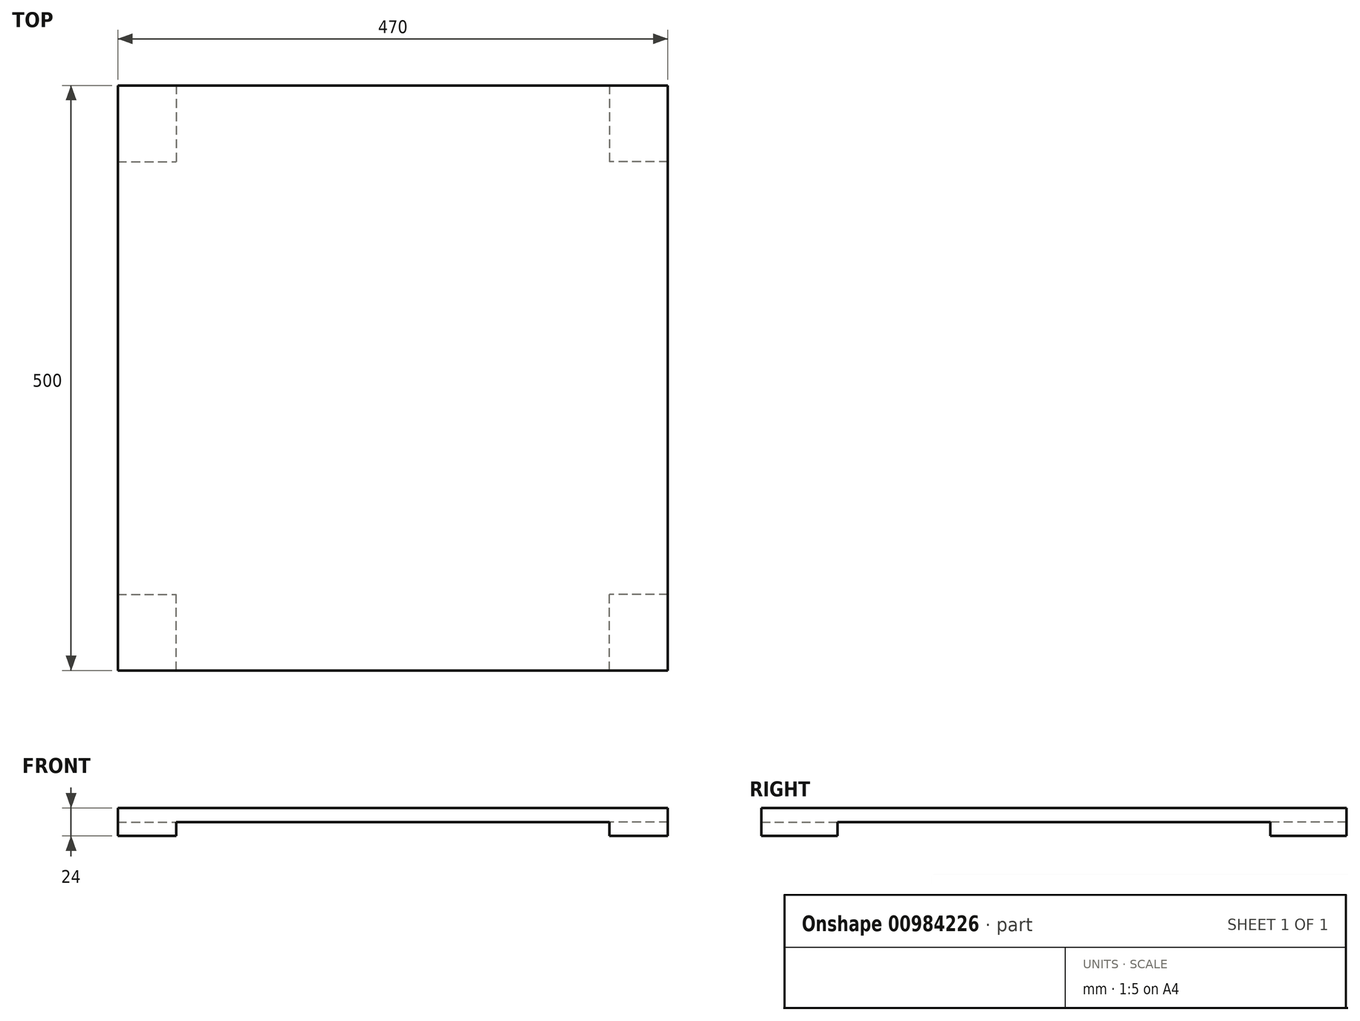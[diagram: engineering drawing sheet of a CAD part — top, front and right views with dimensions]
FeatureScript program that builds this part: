
annotation { "Feature Type Name" : "Feature", "Feature Type Description" : "" }
export const myFeature = defineFeature(function(context is Context, id is Id, definition is map)
    precondition{}
    {
        {
            var Q0;
            Q0=qCreatedBy(makeId("Top.planeOp"),FACE);
            var sketch = newSketch(context, id + "F0", { "sketchPlane" : qUnion([Q0])});
            skLineSegment(sketch, "E0.bottom", {"start": v(-264.02, 245.19) * mm, "end": v(205.98, 245.19) * mm});
            skLineSegment(sketch, "E0.top", {"start": v(-264.02, -254.81) * mm, "end": v(205.98, -254.81) * mm});
            skLineSegment(sketch, "E0.left", {"start": v(-264.02, 245.19) * mm, "end": v(-264.02, -254.81) * mm});
            skLineSegment(sketch, "E0.right", {"start": v(205.98, 245.19) * mm, "end": v(205.98, -254.81) * mm});
            skSolve(sketch);
        }
        {
            var Q0;
            Q0=makeQuery(id+"F0.imprint","IMPRINT",FACE,{"disambiguationData":[TD([[makeQuery(id+"F0.imprint","IMPRINT",EDGE,{"derivedFrom":sQuery(id+"F0.wireOp",EDGE,"E0.bottom")}),-1.0]])]});
            extrude(context, id + "F1", {"entities" : qUnion([Q0]), "oppositeDirection" : true, "depth" : 12 * mm, "offsetDistance" : 25 * mm});
        }
        {
            var Q0;
            Q0=makeQuery(id+"F1.opExtrude","CAP_FACE",FACE,{"disambiguationData":[OSD([sQuery(id+"F0.wireOp",EDGE,"E0.bottom"),sQuery(id+"F0.wireOp",EDGE,"E0.top"),sQuery(id+"F0.wireOp",EDGE,"E0.left"),sQuery(id+"F0.wireOp",EDGE,"E0.right")])],"isStart":false});
            var sketch = newSketch(context, id + "F2", { "sketchPlane" : qUnion([Q0])});
            skLineSegment(sketch, "E1.bottom", {"start": v(205.98, -245.19) * mm, "end": v(155.98, -245.19) * mm});
            skLineSegment(sketch, "E1.top", {"start": v(205.98, -180.19) * mm, "end": v(155.98, -180.19) * mm});
            skLineSegment(sketch, "E1.left", {"start": v(205.98, -245.19) * mm, "end": v(205.98, -180.19) * mm});
            skLineSegment(sketch, "E1.right", {"start": v(155.98, -245.19) * mm, "end": v(155.98, -180.19) * mm});
            skLineSegment(sketch, "E2.bottom", {"start": v(-264.02, -245.19) * mm, "end": v(-214.02, -245.19) * mm});
            skLineSegment(sketch, "E2.top", {"start": v(-264.02, -180.19) * mm, "end": v(-214.02, -180.19) * mm});
            skLineSegment(sketch, "E2.left", {"start": v(-264.02, -245.19) * mm, "end": v(-264.02, -180.19) * mm});
            skLineSegment(sketch, "E2.right", {"start": v(-214.02, -245.19) * mm, "end": v(-214.02, -180.19) * mm});
            skLineSegment(sketch, "E3.bottom", {"start": v(205.98, 254.81) * mm, "end": v(155.98, 254.81) * mm});
            skLineSegment(sketch, "E3.top", {"start": v(205.98, 189.81) * mm, "end": v(155.98, 189.81) * mm});
            skLineSegment(sketch, "E3.left", {"start": v(205.98, 254.81) * mm, "end": v(205.98, 189.81) * mm});
            skLineSegment(sketch, "E3.right", {"start": v(155.98, 254.81) * mm, "end": v(155.98, 189.81) * mm});
            skLineSegment(sketch, "E4.bottom", {"start": v(-264.02, 254.81) * mm, "end": v(-214.02, 254.81) * mm});
            skLineSegment(sketch, "E4.top", {"start": v(-264.02, 189.81) * mm, "end": v(-214.02, 189.81) * mm});
            skLineSegment(sketch, "E4.left", {"start": v(-264.02, 254.81) * mm, "end": v(-264.02, 189.81) * mm});
            skLineSegment(sketch, "E4.right", {"start": v(-214.02, 254.81) * mm, "end": v(-214.02, 189.81) * mm});
            skSolve(sketch);
        }
        {
            var Q0;
            Q0=makeQuery(id+"F2.imprint","IMPRINT",FACE,{"disambiguationData":[TD([[makeQuery(id+"F2.imprint","IMPRINT",EDGE,{"derivedFrom":sQuery(id+"F2.wireOp",EDGE,"E1.bottom")}),1.0]])]});
            var Q1;
            Q1=makeQuery(id+"F2.imprint","IMPRINT",FACE,{"disambiguationData":[TD([[makeQuery(id+"F2.imprint","IMPRINT",EDGE,{"derivedFrom":sQuery(id+"F2.wireOp",EDGE,"E2.bottom")}),1.0]])]});
            var Q2;
            Q2=makeQuery(id+"F2.imprint","IMPRINT",FACE,{"disambiguationData":[TD([[makeQuery(id+"F2.imprint","IMPRINT",EDGE,{"derivedFrom":sQuery(id+"F2.wireOp",EDGE,"E4.bottom")}),-1.0]])]});
            var Q3;
            Q3=makeQuery(id+"F2.imprint","IMPRINT",FACE,{"disambiguationData":[TD([[makeQuery(id+"F2.imprint","IMPRINT",EDGE,{"derivedFrom":sQuery(id+"F2.wireOp",EDGE,"E3.bottom")}),-1.0]])]});
            extrude(context, id + "F3", {"entities" : qUnion([Q0, Q1, Q2, Q3]), "operationType" : NewBodyOperationType.ADD, "depth" : 12 * mm, "offsetDistance" : 25 * mm});
        }
    });
